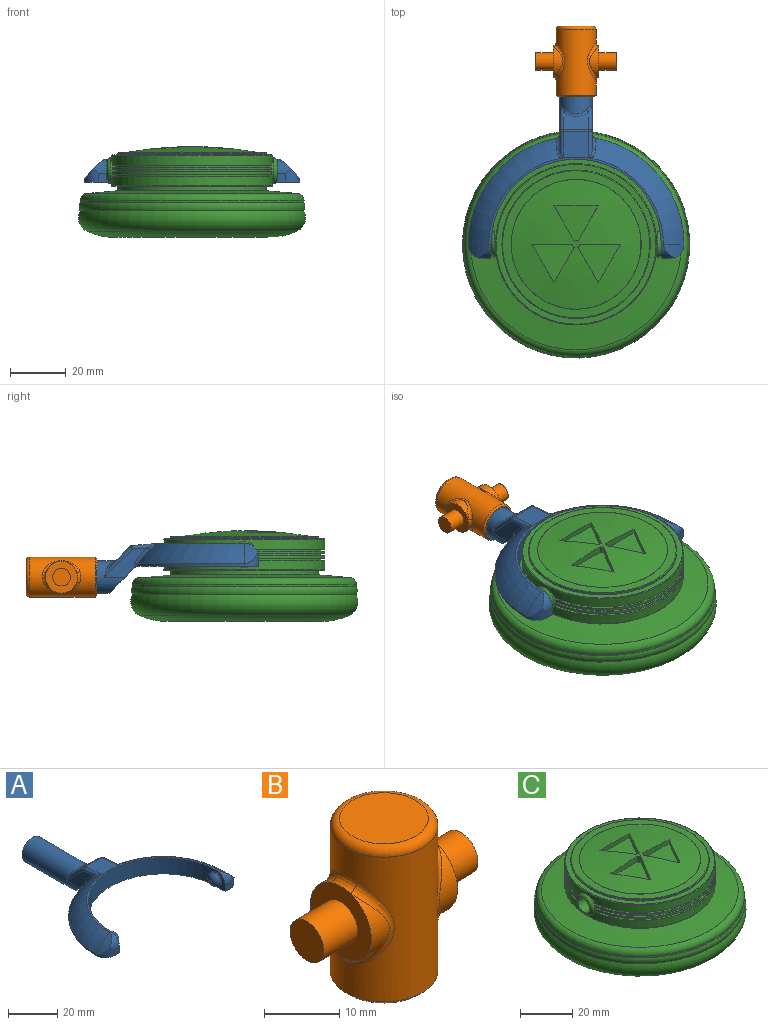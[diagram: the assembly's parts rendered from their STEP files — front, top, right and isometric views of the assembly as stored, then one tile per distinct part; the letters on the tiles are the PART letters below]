
ASSEMBLY  parts=3 mates=2
PART A: 48 faces, bbox 77.3x80.8x18.2 mm
  f0: plane 11.99x9.83mm, normal (0,-0.71,-0.71), area 141.5mm2, adj f1,f2,f9,f30,f43,f46
  f1: plane 15.39x10.49mm, normal (-1,0,0), area 63.5mm2, adj f0,f30,f32,f36,f46,f47
  f2: plane 15.39x10.49mm, normal (1,0,0), area 63.5mm2, adj f0,f30,f34,f39,f43,f44
  f3: plane 9.14x6.37mm, normal (0,0.71,0.71), area 67.6mm2, adj f35,f36,f39,f40
  f4: cylinder r=38.61mm len=37.99mm, axis (0,0,-1), area 42.6mm2, adj f6,f9,f17,f46,f47
  f5: torus R=19.3mm, axis (0,0,-1), area 507.8mm2, adj f10,f11,f12,f29,f42,f44
  f6: torus R=19.3mm, axis (0,0,-1), area 507.8mm2, adj f4,f11,f15,f28,f45,f47
  f7: cylinder r=30.48mm len=60.96mm, axis (0,0,-1), area 746.6mm2, adj f8,f9,f11,f14,f21,f24
  f8: plane 8.13x5.08mm, normal (-1,0,0), area 19.9mm2, adj f7,f9,f13,f19,f24
  f9: plane 77.22x43.73mm, normal (0,0,-1), area 956.2mm2, adj f0,f4,f7,f8,f10,f13,f14,f16
  f10: cylinder r=38.61mm len=37.99mm, axis (0,0,-1), area 42.6mm2, adj f5,f9,f20,f43,f44
  f11: plane 62.55x30.95mm, normal (0,0,1), area 75mm2, adj f5,f6,f7,f18,f19,f27
  f12: cylinder r=22.71mm len=7.33mm, axis (0,1,0), area 24.8mm2, adj f5,f19,f20
  f13: plane 3.05x3.05mm, normal (0,-1,0), area 9.3mm2, adj f8,f9,f19,f20
  f14: plane 8.13x5.08mm, normal (1,0,0), area 19.9mm2, adj f7,f9,f16,f18,f21
  f15: cylinder r=22.71mm len=7.33mm, axis (0,1,0), area 24.8mm2, adj f6,f17,f18
  f16: plane 3.05x3.05mm, normal (0,-1,0), area 9.3mm2, adj f9,f14,f17,f18
  f17: cylinder r=5.08mm len=5.08mm, axis (0,0,-1), area 21.9mm2, adj f4,f9,f15,f16,f18
  f18: cylinder r=5.08mm len=5.08mm, axis (-1,0,0), area 21.9mm2, adj f11,f14,f15,f16,f17
  f19: cylinder r=5.08mm len=5.08mm, axis (-1,0,0), area 21.9mm2, adj f8,f11,f12,f13,f20
  f20: cylinder r=5.08mm len=5.08mm, axis (0,0,-1), area 21.9mm2, adj f9,f10,f12,f13,f19
  f21: cylinder r=3.17mm len=6.35mm, axis (-1,0,0), area 12.7mm2, adj f7,f14,f23
  f22: plane 1.27x1.27mm, normal (1,0,0), area 1.3mm2, adj f23
  f23: torus R=0.64mm, axis (1,0,0), area 56.5mm2, adj f21,f22
  f24: cylinder r=3.17mm len=6.35mm, axis (1,0,0), area 12.7mm2, adj f7,f8,f26
  f25: plane 1.27x1.27mm, normal (-1,0,0), area 1.3mm2, adj f26
  f26: torus R=0.64mm, axis (-1,0,0), area 56.5mm2, adj f24,f25
  f27: plane 9.86x9.36mm, normal (0,0.09,1), area 85.6mm2, adj f11,f28,f29,f32,f34,f35,f42,f45
  f28: plane 1.04x0.17mm, normal (0,-1,0), area 0mm2, adj f6,f27,f45
  f29: plane 1.04x0.17mm, normal (0,-1,0), area 0mm2, adj f5,f27,f42
  f30: cylinder r=5.84mm len=33.01mm, axis (0,-1,0), area 1029.7mm2, adj f0,f1,f2,f31,f38,f40,f41
  f31: plane 11.68x11.68mm, normal (0,1,0), area 107.2mm2, adj f30
  f32: cylinder r=1.27mm len=9.13mm, axis (0,-1,0.09), area 14.4mm2, adj f1,f27,f33,f45
  f33: sphere r=1.27mm, area 1.5mm2, adj f32,f35,f36
  f34: cylinder r=1.27mm len=9.13mm, axis (0,1,-0.09), area 14.4mm2, adj f2,f27,f37,f42
  f35: cylinder r=1.27mm len=9.14mm, axis (-1,0,0), area 8.1mm2, adj f3,f27,f33,f37
  f36: cylinder r=1.27mm len=10.91mm, axis (0,-0.71,0.71), area 23.1mm2, adj f1,f3,f33,f38
  f37: sphere r=1.27mm, area 1.5mm2, adj f34,f35,f39
  f38: bspline ~4.55x2.75mm, area 2.3mm2, adj f30,f36,f40
  f39: cylinder r=1.27mm len=10.91mm, axis (0,0.71,-0.71), area 23.1mm2, adj f2,f3,f37,f41
  f40: bspline ~9.14x2.56mm, area 10.7mm2, adj f3,f30,f38,f41
  f41: bspline ~5.23x3.53mm, area 2.3mm2, adj f30,f39,f40
  f42: bspline ~4.62x3.14mm, area 5.2mm2, adj f5,f27,f29,f34,f44
  f43: cylinder r=1.27mm len=1.74mm, axis (0,0,-1), area 1.9mm2, adj f0,f2,f9,f10,f44
  f44: bspline ~8.6x7.86mm, area 11.9mm2, adj f2,f5,f10,f42,f43
  f45: bspline ~4.62x3.14mm, area 5.2mm2, adj f6,f27,f28,f32,f47
  f46: cylinder r=1.27mm len=1.74mm, axis (0,0,-1), area 1.9mm2, adj f0,f1,f4,f9,f47
  f47: bspline ~8.6x7.86mm, area 11.9mm2, adj f1,f4,f6,f45,f46
PART B: 25 faces, bbox 28.9x15.5x25.4 mm
  f0: cylinder r=5.71mm len=10.81mm, axis (-1,0,0), area 26.2mm2, adj f5,f15
  f1: cylinder r=5.71mm len=10.81mm, axis (-1,0,0), area 26.2mm2, adj f8,f11
  f2: cylinder r=7.14mm len=23.5mm, axis (0,0,-1), area 763.2mm2, adj f9,f10,f11,f12,f13,f14,f15,f16
  f3: plane 11.75x11.75mm, normal (0,0,1), area 108.4mm2, adj f17
  f4: plane 13.02x13.02mm, normal (0,0,-1), area 16.3mm2, adj f22,f24
  f5: plane 11.46x11.46mm, normal (1,0,0), area 70.9mm2, adj f0,f6,f13,f16,f18
  f6: cylinder r=5.71mm len=10.81mm, axis (-1,0,0), area 26.2mm2, adj f5,f14
  f7: cylinder r=5.71mm len=10.81mm, axis (-1,0,0), area 26.2mm2, adj f8,f10
  f8: plane 11.46x11.46mm, normal (-1,0,0), area 70.9mm2, adj f1,f7,f9,f12,f20
  f9: bspline ~4.64x1.73mm, area 6.5mm2, adj f2,f8,f10,f11
  f10: bspline ~13.62x4.91mm, area 20.7mm2, adj f2,f7,f9,f12
  f11: bspline ~13.6x4.87mm, area 20.7mm2, adj f1,f2,f9,f12
  f12: bspline ~4.64x1.73mm, area 6.5mm2, adj f2,f8,f10,f11
  f13: bspline ~4.64x1.73mm, area 6.5mm2, adj f2,f5,f14,f15
  f14: bspline ~13.62x4.91mm, area 20.7mm2, adj f2,f6,f13,f16
  f15: bspline ~13.6x4.87mm, area 20.7mm2, adj f0,f2,f13,f16
  f16: bspline ~4.64x1.73mm, area 6.5mm2, adj f2,f5,f14,f15
  f17: torus R=5.87mm, axis (0,0,1), area 83.8mm2, adj f2,f3
  f18: cylinder r=3.17mm len=6.35mm, axis (-1,0,0), area 126.7mm2, adj f5,f19
  f19: plane 6.35x6.35mm, normal (1,0,0), area 31.7mm2, adj f18
  f20: cylinder r=3.17mm len=6.35mm, axis (1,0,0), area 126.7mm2, adj f8,f21
  f21: plane 6.35x6.35mm, normal (-1,0,0), area 31.7mm2, adj f20
  f22: cylinder r=6.1mm len=22.86mm, axis (0,0,-1), area 875.6mm2, adj f4,f23
  f23: plane 12.19x12.19mm, normal (0,0,-1), area 116.7mm2, adj f22
  f24: cone r=7.14mm half-angle=45deg, axis (0,0,1), area 38.5mm2, adj f2,f4
PART C: 64 faces, bbox 96.3x96.3x32.5 mm
  f0: cylinder r=28.87mm len=57.73mm, axis (0,0,-1), area 595.8mm2, adj f1,f2,f54,f55,f60
  f1: plane 57.13x24.71mm, normal (0,0,1), area 102mm2, adj f0,f3,f54,f55
  f2: plane 57.13x24.71mm, normal (0,0,1), area 102mm2, adj f0,f4,f54,f55
  f3: cylinder r=27.6mm len=54.56mm, axis (0,0,-1), area 49.6mm2, adj f1,f6,f54,f55
  f4: cylinder r=27.6mm len=54.56mm, axis (0,0,-1), area 49.6mm2, adj f2,f5,f54,f55
  f5: plane 57.06x24.48mm, normal (0,0,-1), area 101.4mm2, adj f4,f8,f54,f55
  f6: plane 57.06x24.48mm, normal (0,0,-1), area 101.4mm2, adj f3,f7,f54,f55
  f7: cylinder r=28.87mm len=57.06mm, axis (0,0,-1), area 77.8mm2, adj f6,f14,f54,f55
  f8: cylinder r=28.87mm len=57.06mm, axis (0,0,-1), area 77.8mm2, adj f5,f13,f54,f55
  f9: cylinder r=27.6mm len=54.44mm, axis (0,0,-1), area 49.2mm2, adj f11,f14,f54,f55
  f10: cylinder r=27.6mm len=54.44mm, axis (0,0,-1), area 49.2mm2, adj f12,f13,f54,f55
  f11: plane 57.01x24.31mm, normal (0,0,-1), area 101mm2, adj f9,f15,f54,f55
  f12: plane 57.01x24.31mm, normal (0,0,-1), area 101mm2, adj f10,f16,f54,f55
  f13: plane 57.01x24.31mm, normal (0,0,1), area 101mm2, adj f8,f10,f54,f55
  f14: plane 57.01x24.31mm, normal (0,0,1), area 101mm2, adj f7,f9,f54,f55
  f15: cylinder r=28.87mm len=57.06mm, axis (0,0,-1), area 77.8mm2, adj f11,f17,f54,f55
  f16: cylinder r=28.87mm len=57.06mm, axis (0,0,-1), area 77.8mm2, adj f12,f18,f54,f55
  f17: plane 57.06x24.48mm, normal (0,0,1), area 101.4mm2, adj f15,f19,f54,f55
  f18: plane 57.06x24.48mm, normal (0,0,1), area 101.4mm2, adj f16,f20,f54,f55
  f19: cylinder r=27.6mm len=54.56mm, axis (0,0,-1), area 49.6mm2, adj f17,f22,f54,f55
  f20: cylinder r=27.6mm len=54.56mm, axis (0,0,-1), area 49.6mm2, adj f18,f21,f54,f55
  f21: plane 57.13x24.71mm, normal (0,0,-1), area 102mm2, adj f20,f23,f54,f55
  f22: plane 57.13x24.71mm, normal (0,0,-1), area 102mm2, adj f19,f23,f54,f55
  f23: cylinder r=28.87mm len=57.73mm, axis (0,0,-1), area 595.8mm2, adj f21,f22,f54,f55,f61
  f24: sphere r=135.39mm, area 1385.3mm2, adj f38,f39,f40,f41,f43,f44,f45,f46
  f25: plane 39.35x39.35mm, normal (0,0,-1), area 1216.2mm2, adj f26
  f26: torus R=20.13mm, axis (0,0,-1), area 1430.4mm2, adj f25,f27
  f27: torus R=27.75mm, axis (0,0,-1), area 3543.7mm2, adj f26,f28
  f28: torus R=35.37mm, axis (0,0,-1), area 2180.8mm2, adj f27,f29
  f29: torus R=37.36mm, axis (0,0,-1), area 734.8mm2, adj f28,f30
  f30: cylinder r=40.07mm len=80.14mm, axis (0,0,-1), area 213.4mm2, adj f29,f34
  f31: cone r=26.58mm half-angle=85deg, axis (0,0,-1), area 2265.9mm2, adj f32,f34
  f32: cylinder r=26.58mm len=53.16mm, axis (0,0,-1), area 265.1mm2, adj f31,f33
  f33: plane 57.23x57.23mm, normal (0,0,-1), area 352.3mm2, adj f32,f60
  f34: torus R=37.53mm, axis (0,0,1), area 928.9mm2, adj f30,f31
  f35: cone r=26.58mm half-angle=87deg, axis (0,0,-1), area 477.5mm2, adj f62,f63
  f36: cylinder r=26.58mm len=53.16mm, axis (0,0,-1), area 92.3mm2, adj f37,f62
  f37: plane 57.23x57.23mm, normal (0,0,1), area 352.3mm2, adj f36,f61
  f38: plane 14.61x2.53mm, normal (0,-1,0), area 32.2mm2, adj f24,f39,f41,f42
  f39: plane 13.75x7.94mm, normal (0.87,0.5,0), area 28mm2, adj f24,f38,f40,f42
  f40: plane 12.65x7.3mm, normal (-0.87,0.5,0), area 32.2mm2, adj f24,f39,f41,f42
  f41: cylinder r=1.27mm len=2.53mm, axis (0,0,1), area 3.4mm2, adj f24,f38,f40,f42
  f42: plane 15.24x13.75mm, normal (0,0,1), area 108.3mm2, adj f38,f39,f40,f41
  f43: cylinder r=1.27mm len=2.53mm, axis (0,0,1), area 3.4mm2, adj f24,f44,f46,f47
  f44: plane 12.65x7.3mm, normal (0.87,0.5,0), area 32.2mm2, adj f24,f43,f45,f47
  f45: plane 13.75x7.94mm, normal (-0.87,0.5,0), area 28mm2, adj f24,f44,f46,f47
  f46: plane 14.61x2.53mm, normal (0,-1,0), area 32.2mm2, adj f24,f43,f45,f47
  f47: plane 15.24x13.75mm, normal (0,0,1), area 108.3mm2, adj f43,f44,f45,f46
  f48: cylinder r=1.27mm len=2.53mm, axis (0,0,1), area 3.4mm2, adj f24,f49,f51,f52
  f49: plane 12.65x7.3mm, normal (-0.87,0.5,0), area 32.2mm2, adj f24,f48,f50,f52
  f50: plane 15.88x1.84mm, normal (0,-1,0), area 28mm2, adj f24,f49,f51,f52
  f51: plane 12.65x7.3mm, normal (0.87,0.5,0), area 32.2mm2, adj f24,f48,f50,f52
  f52: plane 15.88x12.65mm, normal (0,0,1), area 108.3mm2, adj f48,f49,f50,f51
  f53: plane 6.6x6.6mm, normal (1,0,0), area 2.6mm2, adj f58,f59
  f54: cylinder r=4.57mm len=9.14mm, axis (-1,0,0), area 20.2mm2, adj f0,f1,f2,f3,f4,f5,f6,f7
  f55: cylinder r=4.57mm len=9.14mm, axis (-1,0,0), area 20.2mm2, adj f0,f1,f2,f3,f4,f5,f6,f7
  f56: plane 6.6x6.6mm, normal (-1,0,0), area 2.6mm2, adj f57,f59
  f57: torus R=3.3mm, axis (1,0,0), area 51.5mm2, adj f55,f56
  f58: torus R=3.3mm, axis (1,0,0), area 51.5mm2, adj f53,f54
  f59: cylinder r=3.17mm len=60.96mm, axis (1,0,0), area 1216.1mm2, adj f53,f56
  f60: torus R=28.61mm, axis (0,0,1), area 72.1mm2, adj f0,f33
  f61: torus R=28.61mm, axis (0,0,-1), area 72.1mm2, adj f23,f37
  f62: torus R=26.33mm, axis (0,0,1), area 64.2mm2, adj f35,f36
  f63: torus R=23.29mm, axis (0,0,1), area 4.5mm2, adj f24,f35
PLACE A t=(32.34,27.52,20.85)mm
PLACE B rot(axis=(-1,0,0),90deg) t=(32.34,80.3,16.88)mm
PLACE C t=(32.34,27.52,33.52)mm
MATE revolute A.f24 <-> C.f54  axis (-1,0,0) through (62.82,27.52,24.92)mm
MATE revolute B.f2 <-> A.f30  axis (0,-1,0) through (32.34,103.16,16.88)mm
